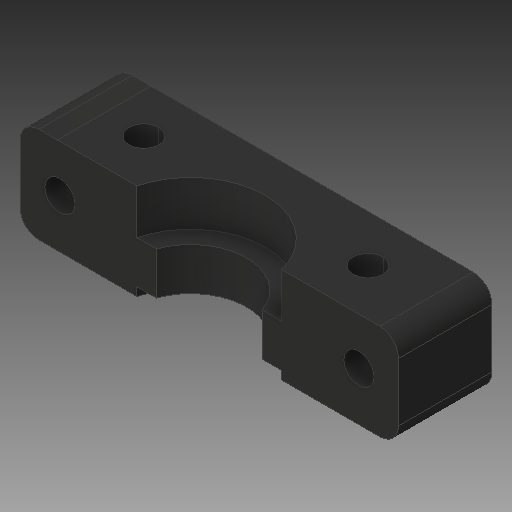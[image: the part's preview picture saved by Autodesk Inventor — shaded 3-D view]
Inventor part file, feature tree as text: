
AUTODESK INVENTOR PART (.ipt)
format: ipt  version: 2018 (Build 220112000, 112)  size: 247,808 bytes
history: native  units: in
note: dims shown in document units (in); Inventor stores cm internally (conversion verified against a paired STEP export)
features: sketch x9, extrude x7, projected_geometry x3, other x3, hole x1, reference x1
ambient origin geometry x8: Origin, YZ Plane, XZ Plane, XY Plane, X Axis, Y Axis, Z Axis, Center Point
bodies: Solid1 (feature_tree)
feature tree (24):
  extrude  "Extrusion1"  Depth=0.0787in
  extrude  "Extrusion2"  Depth=0.0787in
  extrude  "Extrusion3"  Depth=0.189in TaperAngle=0.0deg
  extrude  "Extrusion4"  Depth=0.189in TaperAngle=0.0deg
  hole  "Hole1"  [1 undecoded]
  extrude  "Extrusion5"  Depth=0.0394in
  sketch  "Sketch7"  dims[d17=0.0394in]
  sketch  "Sketch8"  dims[d18=0.126in d19=0.2362in d20=0.1575in d21=0.0787in d22=90.0deg d23=0.315in d24=0.8108in d25=0.1122in]
  extrude  "Extrusion6"  Depth=0.315in
  extrude  "Extrusion7"  Depth=0.1181in TaperAngle=0.0deg
  sketch  "Sketch1"  dims[d1=0.0787in d2=0.0787in]
  reference  "Reference1"
  sketch  "Sketch2"  dims[d3=0.3937in d4=0.0in d5=0.0787in]
  sketch  "Sketch3"  dims[d6=0.6299in d7=0.189in d8=0.0in]
  sketch  "Sketch4"  dims[d9=0.4724in d10=0.189in d11=0.0in]
  sketch  "Sketch5"  dims[d12=0.6299in d13=0.0354in d14=0.0in]
  sketch  "Sketch6"  dims[d15=0.1969in d16=0.0394in]
  projected_geometry  "Projected Loop1"
  projected_geometry  "Projected Loop2"
  sketch  "Sketch9"  dims[d26=0.1122in d27=0.1181in d28=0.0in d29=0.1181in d30=0.0in d31=0.1181in d32=0.0in]
  projected_geometry  "Projected Loop3"
  other  "<userpath>\OneDrive\Inventor\Beast 3D Printer\Hotend Mount Assembly.iam"
  other  "Hotend Mount Assembly.iam"
  other  "Hotend Slide Part 1:1"
note: 1 required parameter value undecoded (feature->parameter linkage not recoverable at this tier; creation-order binding heuristic only, values carry confidence <= 0.55)
